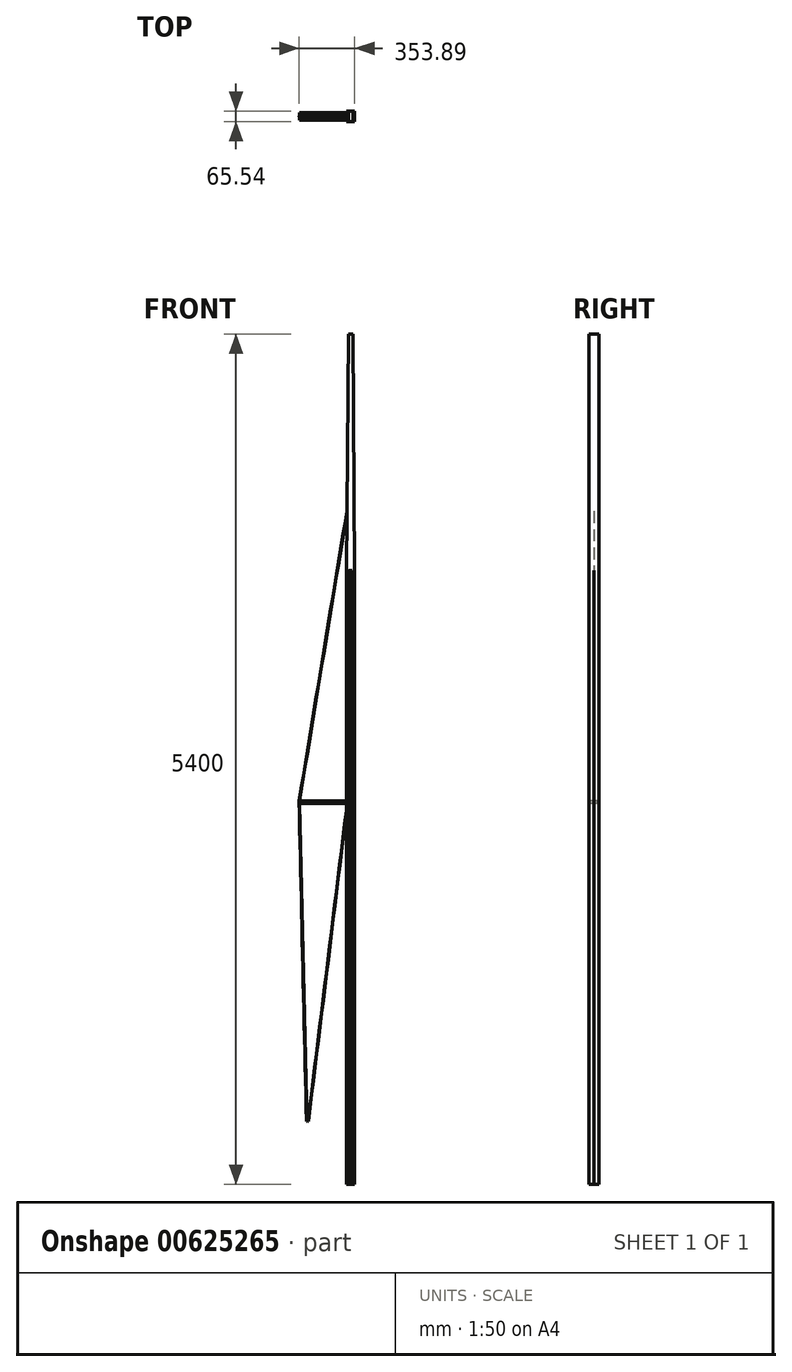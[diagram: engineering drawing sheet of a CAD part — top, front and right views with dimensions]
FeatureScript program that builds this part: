
annotation { "Feature Type Name" : "Feature", "Feature Type Description" : "" }
export const myFeature = defineFeature(function(context is Context, id is Id, definition is map)
    precondition{}
    {
        {
            var Q0;
            Q0=qCreatedBy(makeId("Top.planeOp"),FACE);
            var sketch = newSketch(context, id + "F0", { "sketchPlane" : qUnion([Q0])});
            skPoint(sketch, "E0", {"position": v(0, 3526) * mm});
            skSolve(sketch);
        }
        {
            var Q0;
            Q0=qCreatedBy(makeId("Top.planeOp"),FACE);
            var sketch = newSketch(context, id + "F1", { "sketchPlane" : qUnion([Q0])});
            skPoint(sketch, "E1", {"position": v(0, 1966) * mm});
            skSolve(sketch);
        }
        {
            var Q0;
            Q0=qCreatedBy(makeId("Right.planeOp"),FACE);
            var sketch = newSketch(context, id + "F2", { "sketchPlane" : qUnion([Q0])});
            skLineSegment(sketch, "E2", {"start": v(1966, 0) * mm, "end": v(1966, 5000) * mm});
            skSolve(sketch);
        }
        {
            var Q0;
            Q0=qCreatedBy(makeId("Right.planeOp"),FACE);
            var sketch = newSketch(context, id + "F3", { "sketchPlane" : qUnion([Q0])});
            skPoint(sketch, "E3", {"position": v(1966, 3750) * mm});
            skSolve(sketch);
        }
        {
            var Q0;
            Q0=qCreatedBy(makeId("Right.planeOp"),FACE);
            var sketch = newSketch(context, id + "F4", { "sketchPlane" : qUnion([Q0])});
            skLineSegment(sketch, "E4", {"start": v(1966, 3750) * mm, "end": v(3526, 0) * mm});
            skSolve(sketch);
        }
        {
            var Q0;
            Q0=qCreatedBy(makeId("Top.planeOp"),FACE);
            var sketch = newSketch(context, id + "F5", { "sketchPlane" : qUnion([Q0])});
            skLineSegment(sketch, "E5.bottom", {"start": v(0, 0) * mm, "end": v(-240, 0) * mm});
            skLineSegment(sketch, "E5.top", {"start": v(0, 1902) * mm, "end": v(-240, 1902) * mm});
            skLineSegment(sketch, "E5.left", {"start": v(0, 0) * mm, "end": v(0, 1902) * mm});
            skLineSegment(sketch, "E5.right", {"start": v(-240, 0) * mm, "end": v(-240, 1902) * mm});
            skSolve(sketch);
        }
        {
            var Q0;
            Q0=qCreatedBy(makeId("Top.planeOp"),FACE);
            var sketch = newSketch(context, id + "F6", { "sketchPlane" : qUnion([Q0])});
            skLineSegment(sketch, "E6.bottom", {"start": v(0, 0) * mm, "end": v(-280, 0) * mm});
            skLineSegment(sketch, "E6.top", {"start": v(0, 1982) * mm, "end": v(-280, 1982) * mm});
            skLineSegment(sketch, "E6.left", {"start": v(0, 0) * mm, "end": v(0, 1982) * mm});
            skLineSegment(sketch, "E6.right", {"start": v(-280, 0) * mm, "end": v(-280, 1982) * mm});
            skSolve(sketch);
        }
        {
            var Q0;
            Q0=qCreatedBy(makeId("Top.planeOp"),FACE);
            var sketch = newSketch(context, id + "F7", { "sketchPlane" : qUnion([Q0])});
            skLineSegment(sketch, "E7.bottom", {"start": v(-280, 1982) * mm, "end": v(-240, 1982) * mm});
            skLineSegment(sketch, "E7.top", {"start": v(-280, 1902) * mm, "end": v(-240, 1902) * mm});
            skLineSegment(sketch, "E7.left", {"start": v(-280, 1982) * mm, "end": v(-280, 1902) * mm});
            skLineSegment(sketch, "E7.right", {"start": v(-240, 1982) * mm, "end": v(-240, 1902) * mm});
            skSolve(sketch);
        }
        {
            var Q0;
            Q0=qCreatedBy(makeId("Right.planeOp"),FACE);
            var sketch = newSketch(context, id + "F8", { "sketchPlane" : qUnion([Q0])});
            skPoint(sketch, "E8", {"position": v(1966, 2000) * mm});
            skSolve(sketch);
        }
        {
            var Q0;
            Q0=qCreatedBy(makeId("Right.planeOp"),FACE);
            var sketch = newSketch(context, id + "F9", { "sketchPlane" : qUnion([Q0])});
            skLineSegment(sketch, "E9", {"start": v(3526, 0) * mm, "end": v(1966, 0) * mm});
            skSolve(sketch);
        }
        {
            var Q0;
            Q0=qCreatedBy(makeId("Top.planeOp"),FACE);
            cPlane(context, id + "F10", {"entities" : qUnion([Q0]), "cplaneType" : CPlaneType.OFFSET, "offset" : 2000 * mm, "width" : 150 * mm, "height" : 150 * mm});
        }
        {
            var Q0;
            Q0=qCreatedBy(id+"F10.planeOp",FACE);
            var sketch = newSketch(context, id + "F11", { "sketchPlane" : qUnion([Q0])});
            skCircle(sketch, "E10", {"center": v(0, 1966) * mm, "radius": 200 * mm});
            skSolve(sketch);
        }
        {
            var Q0;
            Q0=qCreatedBy(makeId("Front.planeOp"),FACE);
            cPlane(context, id + "F12", {"entities" : qUnion([Q0]), "cplaneType" : CPlaneType.OFFSET, "offset" : 1933 * mm, "oppositeDirection" : true, "width" : 150 * mm, "height" : 150 * mm});
        }
        {
            var Q0;
            Q0=qCreatedBy(makeId("Right.planeOp"),FACE);
            var sketch = newSketch(context, id + "F13", { "sketchPlane" : qUnion([Q0])});
            skPoint(sketch, "E11", {"position": v(1966, 2050) * mm});
            skSolve(sketch);
        }
        {
            var Q0;
            Q0=qCreatedBy(makeId("Top.planeOp"),FACE);
            var sketch = newSketch(context, id + "F14", { "sketchPlane" : qUnion([Q0])});
            skLineSegment(sketch, "E12.bottom", {"start": v(-26, 1966) * mm, "end": v(0, 1966) * mm});
            skLineSegment(sketch, "E12.top", {"start": v(-26, 1900.5) * mm, "end": v(0, 1900.5) * mm});
            skLineSegment(sketch, "E12.left", {"start": v(-26, 1966) * mm, "end": v(-26, 1900.5) * mm});
            skLineSegment(sketch, "E12.right", {"start": v(0, 1966) * mm, "end": v(0, 1900.5) * mm});
            skLineSegment(sketch, "E13.bottom", {"start": v(0, 1900.5) * mm, "end": v(26, 1900.5) * mm});
            skLineSegment(sketch, "E13.top", {"start": v(0, 1966) * mm, "end": v(26, 1966) * mm});
            skLineSegment(sketch, "E13.left", {"start": v(0, 1900.5) * mm, "end": v(0, 1966) * mm});
            skLineSegment(sketch, "E13.right", {"start": v(26, 1900.5) * mm, "end": v(26, 1966) * mm});
            skSolve(sketch);
        }
        {
            var Q0;
            Q0=makeQuery(id+"F14.imprint","IMPRINT",FACE,{"disambiguationData":[TD([[makeQuery(id+"F14.imprint","IMPRINT",EDGE,{"derivedFrom":sQuery(id+"F14.wireOp",EDGE,"E12.bottom")}),-1.0]])]});
            extrude(context, id + "F15", {"entities" : qUnion([Q0]), "oppositeDirection" : true, "depth" : 400 * mm, "offsetDistance" : 25 * mm});
        }
        {
            var Q0;
            Q0=makeQuery(id+"F15.opExtrude","CAP_FACE",FACE,{"disambiguationData":[OSD([sQuery(id+"F14.wireOp",EDGE,"E12.bottom"),sQuery(id+"F14.wireOp",EDGE,"E12.top"),sQuery(id+"F14.wireOp",EDGE,"E12.left"),sQuery(id+"F14.wireOp",EDGE,"E13.left")])],"isStart":true});
            extrude(context, id + "F16", {"entities" : qUnion([Q0]), "operationType" : NewBodyOperationType.ADD, "depth" : 3500 * mm, "offsetDistance" : 25 * mm});
        }
        {
            var Q0;
            Q0=makeQuery(id+"F15.opExtrude","SWEPT_BODY",BODY,{"disambiguationData":[OSD([sQuery(id+"F14.wireOp",EDGE,"E12.bottom"),sQuery(id+"F14.wireOp",EDGE,"E12.top"),sQuery(id+"F14.wireOp",EDGE,"E12.left"),sQuery(id+"F14.wireOp",EDGE,"E13.left")])]});
            var Q1;
            Q1=qCreatedBy(makeId("Right.planeOp"),FACE);
            mirror(context, id + "F17", {"operationType" : NewBodyOperationType.ADD, "entities" : qUnion([Q0]), "mirrorPlane" : qUnion([Q1])});
        }
        {
            var Q0;
            Q0=qCreatedBy(makeId("Top.planeOp"),FACE);
            cPlane(context, id + "F18", {"entities" : qUnion([Q0]), "cplaneType" : CPlaneType.OFFSET, "offset" : 5000 * mm, "width" : 150 * mm, "height" : 150 * mm});
        }
        {
            var Q0;
            Q0=qCreatedBy(id+"F18.planeOp",FACE);
            var sketch = newSketch(context, id + "F19", { "sketchPlane" : qUnion([Q0])});
            skLineSegment(sketch, "E14.bottom", {"start": v(-14, 1966) * mm, "end": v(14, 1966) * mm});
            skLineSegment(sketch, "E14.top", {"start": v(-14, 1900.5) * mm, "end": v(14, 1900.5) * mm});
            skLineSegment(sketch, "E14.left", {"start": v(-14, 1966) * mm, "end": v(-14, 1900.5) * mm});
            skLineSegment(sketch, "E14.right", {"start": v(14, 1966) * mm, "end": v(14, 1900.5) * mm});
            skSolve(sketch);
        }
        {
            var Q1;
            Q1=makeQuery(id+"F19.imprint","IMPRINT",FACE,{"disambiguationData":[TD([[makeQuery(id+"F19.imprint","IMPRINT",EDGE,{"derivedFrom":sQuery(id+"F19.wireOp",EDGE,"E14.bottom")}),-1.0]])]});
            var Q2;
            {var subQ0=makeQuery(id+"F16.opExtrude","CAP_FACE",FACE,{"disambiguationData":[OSD([sQuery(id+"F14.wireOp",EDGE,"E12.bottom"),sQuery(id+"F14.wireOp",EDGE,"E12.top"),sQuery(id+"F14.wireOp",EDGE,"E12.left"),sQuery(id+"F14.wireOp",EDGE,"E13.left")])],"isStart":false});Q2=makeQuery(id+"F17.boolean.opBoolean","MERGE",FACE,{"derivedFrom":[subQ0,makeQuery(id+"F17.opPattern","COPY",FACE,{"derivedFrom":subQ0,"instanceName":"1"})]});}
            loft(context, id + "F20", {"operationType" : NewBodyOperationType.ADD, "sheetProfilesArray" : [{ "sheetProfileEntities" : qUnion([Q1]) }, { "sheetProfileEntities" : qUnion([Q2]) }]});
        }
        {
            var Q0;
            {var subQ0=sQuery(id+"F14.wireOp",EDGE,"E12.left");Q0=makeQuery(id+"F16.boolean.opBoolean","MERGE",FACE,{"derivedFrom":[makeQuery(id+"F15.opExtrude","SWEPT_FACE",FACE,{"disambiguationData":[OSD([subQ0])]}),makeQuery(id+"F16.opExtrude","SWEPT_FACE",FACE,{"disambiguationData":[OSD([subQ0])]})]});}
            var sketch = newSketch(context, id + "F21", { "sketchPlane" : qUnion([Q0])});
            skLineSegment(sketch, "E15.bottom", {"start": v(-1956.28, 2017.77) * mm, "end": v(-1908.33, 2017.77) * mm});
            skLineSegment(sketch, "E15.top", {"start": v(-1956.28, 2035) * mm, "end": v(-1908.33, 2035) * mm});
            skLineSegment(sketch, "E15.left", {"start": v(-1956.28, 2017.77) * mm, "end": v(-1956.28, 2035) * mm});
            skLineSegment(sketch, "E15.right", {"start": v(-1908.33, 2017.77) * mm, "end": v(-1908.33, 2035) * mm});
            skSolve(sketch);
        }
        {
            var Q0;
            Q0=makeQuery(id+"F21.imprint","IMPRINT",FACE,{"disambiguationData":[TD([[makeQuery(id+"F21.imprint","IMPRINT",EDGE,{"derivedFrom":sQuery(id+"F21.wireOp",EDGE,"E15.bottom")}),1.0]])]});
            extrude(context, id + "F22", {"entities" : qUnion([Q0]), "depth" : 300 * mm, "offsetDistance" : 25 * mm});
        }
        {
            var Q0;
            Q0=qCreatedBy(id+"F12.planeOp",FACE);
            var sketch = newSketch(context, id + "F23", { "sketchPlane" : qUnion([Q0])});
            skLineSegment(sketch, "E16", {"start": v(-26, 1973.96) * mm, "end": v(-269.85, 0) * mm});
            skSolve(sketch);
        }
        {
            var Q0;
            Q0=qCreatedBy(id+"F12.planeOp",FACE);
            var sketch = newSketch(context, id + "F24", { "sketchPlane" : qUnion([Q0])});
            skLineSegment(sketch, "E17", {"start": v(-326, 2036.46) * mm, "end": v(-22.99, 3876.38) * mm});
            skSolve(sketch);
        }
        {
            var Q0;
            Q0=qCreatedBy(id+"F12.planeOp",FACE);
            var sketch = newSketch(context, id + "F25", { "sketchPlane" : qUnion([Q0])});
            skLineSegment(sketch, "E18", {"start": v(-326.63, 2035.01) * mm, "end": v(-279.54, 0) * mm});
            skSolve(sketch);
        }
        {
            var Q0;
            Q0=makeQuery(id+"F7.imprint","IMPRINT",FACE,{"disambiguationData":[TD([[makeQuery(id+"F7.imprint","IMPRINT",EDGE,{"derivedFrom":sQuery(id+"F7.wireOp",EDGE,"E7.bottom")}),-1.0]])]});
            var sketch = newSketch(context, id + "F26", { "sketchPlane" : qUnion([Q0])});
            skCircle(sketch, "E19", {"center": v(-269.85, 1933) * mm, "radius": 0.88 * mm});
            skSolve(sketch);
        }
        {
            var Q0;
            Q0 = qSketchRegion(id + "F26", true);
            var Q1;
            Q1=sQuery(id+"F23.wireOp",EDGE,"E16");
            sweep(context, id + "F27", {"operationType" : NewBodyOperationType.ADD, "profiles" : qUnion([Q0]), "path" : qUnion([Q1])});
        }
        {
            var Q0;
            Q0=makeQuery(id+"F7.imprint","IMPRINT",FACE,{"disambiguationData":[TD([[makeQuery(id+"F7.imprint","IMPRINT",EDGE,{"derivedFrom":sQuery(id+"F7.wireOp",EDGE,"E7.bottom")}),-1.0]])]});
            var sketch = newSketch(context, id + "F28", { "sketchPlane" : qUnion([Q0])});
            skCircle(sketch, "E20", {"center": v(-279.54, 1933) * mm, "radius": 1.25 * mm});
            skSolve(sketch);
        }
        {
            var Q0;
            Q0 = qSketchRegion(id + "F28", true);
            var Q1;
            Q1=sQuery(id+"F25.wireOp",EDGE,"E18");
            sweep(context, id + "F29", {"operationType" : NewBodyOperationType.ADD, "profiles" : qUnion([Q0]), "path" : qUnion([Q1])});
        }
        {
            var Q0;
            Q0=makeQuery(id+"F22.opExtrude","SWEPT_FACE",FACE,{"disambiguationData":[OSD([sQuery(id+"F21.wireOp",EDGE,"E15.top")])]});
            var sketch = newSketch(context, id + "F30", { "sketchPlane" : qUnion([Q0])});
            skCircle(sketch, "E21", {"center": v(-326, 1933) * mm, "radius": 1.25 * mm});
            skSolve(sketch);
        }
        {
            var Q0;
            Q0 = qSketchRegion(id + "F30", true);
            var Q1;
            Q1=sQuery(id+"F24.wireOp",EDGE,"E17");
            sweep(context, id + "F31", {"profiles" : qUnion([Q0]), "path" : qUnion([Q1])});
        }
        {
            var Q0;
            Q0=qCreatedBy(makeId("Top.planeOp"),FACE);
            var sketch = newSketch(context, id + "F32", { "sketchPlane" : qUnion([Q0])});
            skLineSegment(sketch, "E22", {"start": v(-8.47, 1902.81) * mm, "end": v(-3.83, 1908.34) * mm});
            skArc(sketch, "E23", {"start": v(-3.83, 1908.34) * mm, "mid": v(0, 1910.13) * mm, "end": v(3.83, 1908.34) * mm});
            skLineSegment(sketch, "E24", {"start": v(3.83, 1908.34) * mm, "end": v(8.47, 1902.81) * mm});
            skLineSegment(sketch, "E25", {"start": v(8.47, 1902.81) * mm, "end": v(8.56, 1902.55) * mm});
            skLineSegment(sketch, "E26", {"start": v(8.56, 1902.55) * mm, "end": v(8.49, 1902.34) * mm});
            skLineSegment(sketch, "E27", {"start": v(8.49, 1902.34) * mm, "end": v(8.15, 1902.1) * mm});
            skLineSegment(sketch, "E28", {"start": v(8.15, 1902.1) * mm, "end": v(7.6, 1902) * mm});
            skLineSegment(sketch, "E29", {"start": v(7.6, 1902) * mm, "end": v(6.65, 1901.96) * mm});
            skLineSegment(sketch, "E30", {"start": v(6.65, 1901.96) * mm, "end": v(3.62, 1901.96) * mm});
            skArc(sketch, "E31", {"start": v(3.62, 1901.96) * mm, "mid": v(1.88, 1901.96) * mm, "end": v(2.75, 1900.46) * mm});
            skLineSegment(sketch, "E32", {"start": v(2.75, 1900.46) * mm, "end": v(6.65, 1900.46) * mm});
            skLineSegment(sketch, "E33", {"start": v(0, 1965.95) * mm, "end": v(-2.32, 1965.82) * mm});
            skLineSegment(sketch, "E34", {"start": v(-2.32, 1965.82) * mm, "end": v(-4.6, 1965.5) * mm});
            skLineSegment(sketch, "E35", {"start": v(-4.6, 1965.5) * mm, "end": v(-6.8, 1964.96) * mm});
            skLineSegment(sketch, "E36", {"start": v(-6.8, 1964.96) * mm, "end": v(-8.79, 1964.3) * mm});
            skLineSegment(sketch, "E37", {"start": v(-8.79, 1964.3) * mm, "end": v(-10.73, 1963.47) * mm});
            skLineSegment(sketch, "E38", {"start": v(-10.73, 1963.47) * mm, "end": v(-12.38, 1962.56) * mm});
            skLineSegment(sketch, "E39", {"start": v(-12.38, 1962.56) * mm, "end": v(-14.04, 1961.5) * mm});
            skLineSegment(sketch, "E40", {"start": v(-14.04, 1961.5) * mm, "end": v(-15.54, 1960.4) * mm});
            skLineSegment(sketch, "E41", {"start": v(-15.54, 1960.4) * mm, "end": v(-16.94, 1959.15) * mm});
            skLineSegment(sketch, "E42", {"start": v(-16.94, 1959.15) * mm, "end": v(-18.38, 1957.57) * mm});
            skLineSegment(sketch, "E43", {"start": v(-18.38, 1957.57) * mm, "end": v(-20.68, 1954.49) * mm});
            skLineSegment(sketch, "E44", {"start": v(-20.68, 1954.49) * mm, "end": v(-22.27, 1951.66) * mm});
            skLineSegment(sketch, "E45", {"start": v(-22.27, 1951.66) * mm, "end": v(-23.3, 1948.96) * mm});
            skLineSegment(sketch, "E46", {"start": v(-23.3, 1948.96) * mm, "end": v(-24.27, 1945.79) * mm});
            skLineSegment(sketch, "E47", {"start": v(-24.27, 1945.79) * mm, "end": v(-25.05, 1942.5) * mm});
            skLineSegment(sketch, "E48", {"start": v(-25.05, 1942.5) * mm, "end": v(-25.55, 1939.43) * mm});
            skLineSegment(sketch, "E49", {"start": v(-25.55, 1939.43) * mm, "end": v(-25.83, 1936.64) * mm});
            skLineSegment(sketch, "E50", {"start": v(-25.83, 1936.64) * mm, "end": v(-26, 1932.73) * mm});
            skLineSegment(sketch, "E51", {"start": v(-26, 1932.73) * mm, "end": v(-25.82, 1928.85) * mm});
            skLineSegment(sketch, "E52", {"start": v(-25.82, 1928.85) * mm, "end": v(-25.21, 1925.05) * mm});
            skLineSegment(sketch, "E53", {"start": v(-25.21, 1925.05) * mm, "end": v(-24.12, 1920.98) * mm});
            skLineSegment(sketch, "E54", {"start": v(-24.12, 1920.98) * mm, "end": v(-22.57, 1916.98) * mm});
            skLineSegment(sketch, "E55", {"start": v(-22.57, 1916.98) * mm, "end": v(-21.52, 1914.78) * mm});
            skLineSegment(sketch, "E56", {"start": v(-21.52, 1914.78) * mm, "end": v(-20.24, 1912.55) * mm});
            skLineSegment(sketch, "E57", {"start": v(-20.24, 1912.55) * mm, "end": v(-18.81, 1910.39) * mm});
            skLineSegment(sketch, "E58", {"start": v(-18.81, 1910.39) * mm, "end": v(-17.38, 1908.44) * mm});
            skLineSegment(sketch, "E59", {"start": v(-17.38, 1908.44) * mm, "end": v(-15.74, 1906.54) * mm});
            skLineSegment(sketch, "E60", {"start": v(-15.74, 1906.54) * mm, "end": v(-14.41, 1905.22) * mm});
            skLineSegment(sketch, "E61", {"start": v(-14.41, 1905.22) * mm, "end": v(-13.03, 1903.94) * mm});
            skLineSegment(sketch, "E62", {"start": v(-13.03, 1903.94) * mm, "end": v(-11.79, 1902.87) * mm});
            skLineSegment(sketch, "E63", {"start": v(-11.79, 1902.87) * mm, "end": v(-10.87, 1902.13) * mm});
            skLineSegment(sketch, "E64", {"start": v(-10.87, 1902.13) * mm, "end": v(-10.2, 1901.65) * mm});
            skLineSegment(sketch, "E65", {"start": v(-10.2, 1901.65) * mm, "end": v(-9.68, 1901.28) * mm});
            skArc(sketch, "E66", {"start": v(6.65, 1900.46) * mm, "mid": v(8.22, 1900.66) * mm, "end": v(9.68, 1901.28) * mm});
            skArc(sketch, "E67", {"start": v(-9.68, 1901.28) * mm, "mid": v(-8.22, 1900.66) * mm, "end": v(-6.65, 1900.46) * mm});
            skLineSegment(sketch, "E68", {"start": v(9.68, 1901.28) * mm, "end": v(10.26, 1901.69) * mm});
            skLineSegment(sketch, "E69", {"start": v(10.26, 1901.69) * mm, "end": v(11.01, 1902.24) * mm});
            skLineSegment(sketch, "E70", {"start": v(11.01, 1902.24) * mm, "end": v(12.1, 1903.13) * mm});
            skLineSegment(sketch, "E71", {"start": v(12.1, 1903.13) * mm, "end": v(13.52, 1904.4) * mm});
            skLineSegment(sketch, "E72", {"start": v(13.52, 1904.4) * mm, "end": v(15.03, 1905.83) * mm});
            skLineSegment(sketch, "E73", {"start": v(15.03, 1905.83) * mm, "end": v(16.37, 1907.23) * mm});
            skLineSegment(sketch, "E74", {"start": v(16.37, 1907.23) * mm, "end": v(17.49, 1908.57) * mm});
            skLineSegment(sketch, "E75", {"start": v(17.49, 1908.57) * mm, "end": v(19.36, 1911.2) * mm});
            skLineSegment(sketch, "E76", {"start": v(19.36, 1911.2) * mm, "end": v(21.15, 1914.1) * mm});
            skLineSegment(sketch, "E77", {"start": v(21.15, 1914.1) * mm, "end": v(22.57, 1916.98) * mm});
            skLineSegment(sketch, "E78", {"start": v(22.57, 1916.98) * mm, "end": v(24.12, 1920.98) * mm});
            skLineSegment(sketch, "E79", {"start": v(24.12, 1920.98) * mm, "end": v(25.21, 1925.05) * mm});
            skLineSegment(sketch, "E80", {"start": v(25.21, 1925.05) * mm, "end": v(25.82, 1928.85) * mm});
            skLineSegment(sketch, "E81", {"start": v(25.82, 1928.85) * mm, "end": v(26, 1932.73) * mm});
            skLineSegment(sketch, "E82", {"start": v(26, 1932.73) * mm, "end": v(25.83, 1936.64) * mm});
            skLineSegment(sketch, "E83", {"start": v(25.83, 1936.64) * mm, "end": v(25.55, 1939.43) * mm});
            skLineSegment(sketch, "E84", {"start": v(25.55, 1939.43) * mm, "end": v(25.05, 1942.5) * mm});
            skLineSegment(sketch, "E85", {"start": v(25.05, 1942.5) * mm, "end": v(24.27, 1945.79) * mm});
            skLineSegment(sketch, "E86", {"start": v(24.27, 1945.79) * mm, "end": v(23.3, 1948.96) * mm});
            skLineSegment(sketch, "E87", {"start": v(23.3, 1948.96) * mm, "end": v(22.27, 1951.66) * mm});
            skLineSegment(sketch, "E88", {"start": v(22.27, 1951.66) * mm, "end": v(20.68, 1954.49) * mm});
            skLineSegment(sketch, "E89", {"start": v(20.68, 1954.49) * mm, "end": v(18.38, 1957.57) * mm});
            skLineSegment(sketch, "E90", {"start": v(18.38, 1957.57) * mm, "end": v(16.35, 1959.7) * mm});
            skLineSegment(sketch, "E91", {"start": v(16.35, 1959.7) * mm, "end": v(14.29, 1961.33) * mm});
            skLineSegment(sketch, "E92", {"start": v(14.29, 1961.33) * mm, "end": v(11.95, 1962.81) * mm});
            skLineSegment(sketch, "E93", {"start": v(11.95, 1962.81) * mm, "end": v(9.67, 1963.96) * mm});
            skLineSegment(sketch, "E94", {"start": v(9.67, 1963.96) * mm, "end": v(7.52, 1964.74) * mm});
            skLineSegment(sketch, "E95", {"start": v(7.52, 1964.74) * mm, "end": v(5.13, 1965.4) * mm});
            skLineSegment(sketch, "E96", {"start": v(5.13, 1965.4) * mm, "end": v(2.59, 1965.8) * mm});
            skLineSegment(sketch, "E97", {"start": v(2.59, 1965.8) * mm, "end": v(0, 1965.95) * mm});
            skLineSegment(sketch, "E98", {"start": v(-6.65, 1900.46) * mm, "end": v(-2.75, 1900.46) * mm});
            skArc(sketch, "E99", {"start": v(-2.75, 1900.46) * mm, "mid": v(-1.88, 1901.96) * mm, "end": v(-3.62, 1901.96) * mm});
            skLineSegment(sketch, "E100", {"start": v(-3.62, 1901.96) * mm, "end": v(-6.65, 1901.96) * mm});
            skLineSegment(sketch, "E101", {"start": v(-6.65, 1901.96) * mm, "end": v(-7.85, 1902.02) * mm});
            skLineSegment(sketch, "E102", {"start": v(-7.85, 1902.02) * mm, "end": v(-8.24, 1902.13) * mm});
            skLineSegment(sketch, "E103", {"start": v(-8.24, 1902.13) * mm, "end": v(-8.49, 1902.34) * mm});
            skLineSegment(sketch, "E104", {"start": v(-8.49, 1902.34) * mm, "end": v(-8.56, 1902.55) * mm});
            skLineSegment(sketch, "E105", {"start": v(-8.56, 1902.55) * mm, "end": v(-8.47, 1902.81) * mm});
            skSolve(sketch);
        }
        {
            var Q0;
            Q0 = qSketchRegion(id + "F32", true);
            extrude(context, id + "F33", {"entities" : qUnion([Q0]), "oppositeDirection" : true, "depth" : 400 * mm, "offsetDistance" : 25 * mm});
        }
        {
            var Q0;
            Q0 = qSketchRegion(id + "F32", true);
            extrude(context, id + "F34", {"entities" : qUnion([Q0]), "operationType" : NewBodyOperationType.ADD, "depth" : 3500 * mm, "offsetDistance" : 25 * mm});
        }
    });
